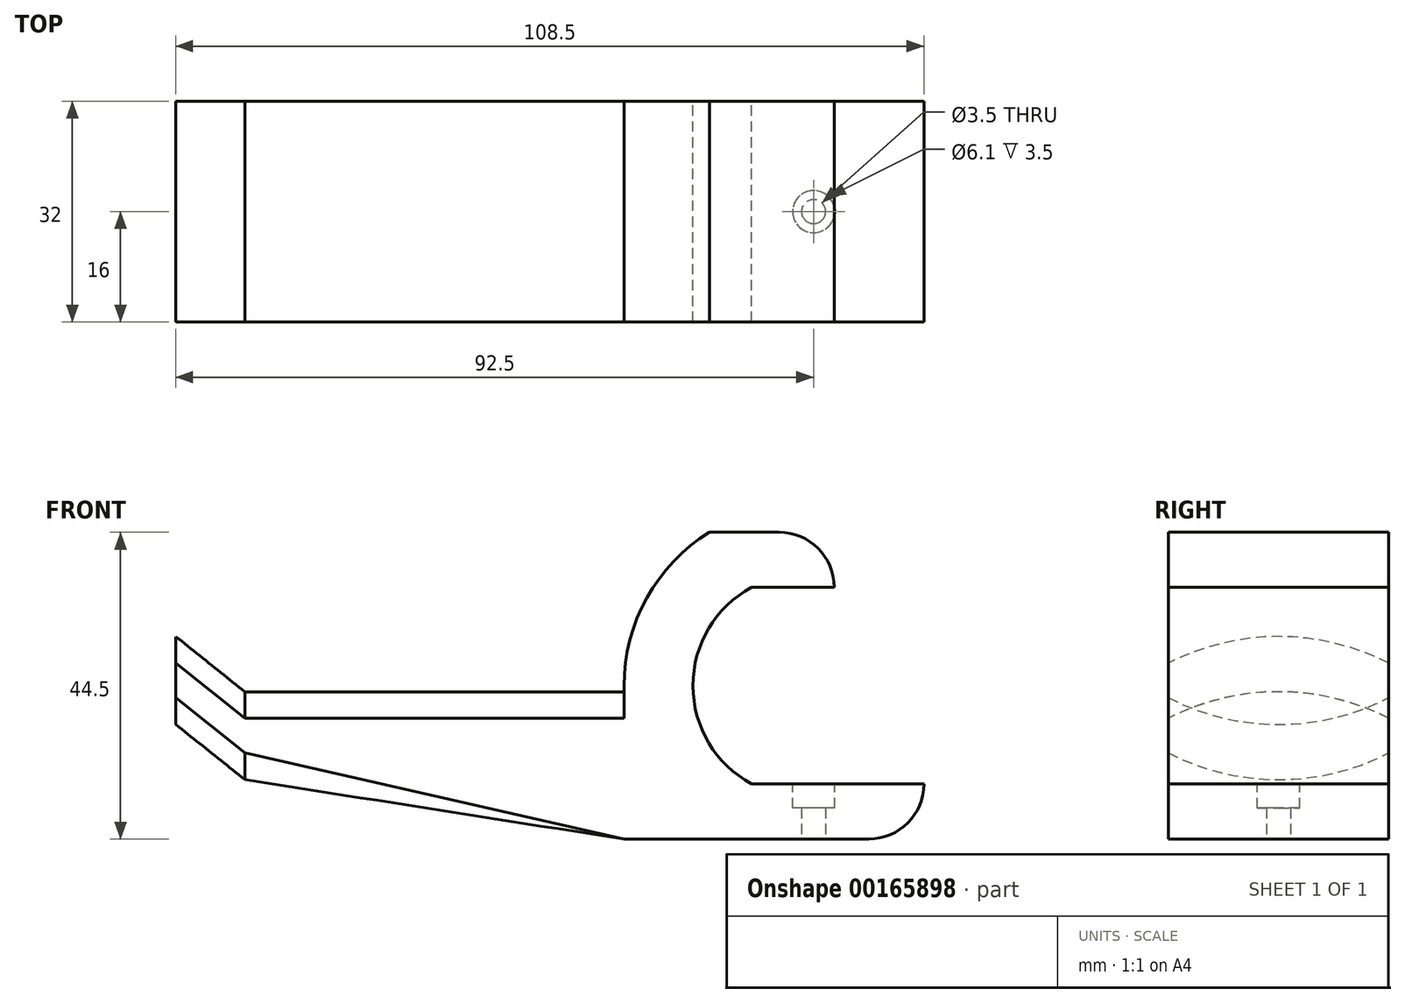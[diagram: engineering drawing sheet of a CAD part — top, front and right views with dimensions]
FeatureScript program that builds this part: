
annotation { "Feature Type Name" : "Feature", "Feature Type Description" : "" }
export const myFeature = defineFeature(function(context is Context, id is Id, definition is map)
    precondition{}
    {
        {
            var Q0;
            Q0=qCreatedBy(makeId("Front.planeOp"),FACE);
            var sketch = newSketch(context, id + "F0", { "sketchPlane" : qUnion([Q0])});
            skArc(sketch, "E0", {"start": v(8.5, 14.25) * mm, "mid": v(0, 0) * mm, "end": v(8.5, -14.25) * mm});
            skLineSegment(sketch, "E1", {"start": v(8.5, 14.25) * mm, "end": v(20.5, 14.25) * mm});
            skLineSegment(sketch, "E2", {"start": v(8.5, -14.25) * mm, "end": v(33.5, -14.25) * mm});
            skArc(sketch, "E3", {"start": v(20.5, 14.25) * mm, "mid": v(18.16, 19.9) * mm, "end": v(12.5, 22.25) * mm});
            skLineSegment(sketch, "E4", {"start": v(12.5, 22.25) * mm, "end": v(2.37, 22.25) * mm});
            skArc(sketch, "E5", {"start": v(2.37, 22.25) * mm, "mid": v(-6.7, 12.73) * mm, "end": v(-10, 0) * mm});
            skArc(sketch, "E6", {"start": v(25.5, -22.25) * mm, "mid": v(31.16, -19.9) * mm, "end": v(33.5, -14.25) * mm});
            skLineSegment(sketch, "E7", {"start": v(25.5, -22.25) * mm, "end": v(-10, -22.25) * mm});
            skLineSegment(sketch, "E8", {"start": v(-10, 0) * mm, "end": v(-10, -22.25) * mm});
            skSolve(sketch);
        }
        {
            var Q0;
            Q0 = qSketchRegion(id + "F0", true);
            extrude(context, id + "F1", {"entities" : qUnion([Q0]), "depth" : 16 * mm, "hasSecondDirection" : true, "secondDirectionOppositeDirection" : true, "secondDirectionDepth" : 16 * mm});
        }
        {
            var Q0;
            Q0=makeQuery(id+"F1.opExtrude","SWEPT_FACE",FACE,{"disambiguationData":[OSD([sQuery(id+"F0.wireOp",EDGE,"E8")])]});
            var sketch = newSketch(context, id + "F2", { "sketchPlane" : qUnion([Q0])});
            skArc(sketch, "E9", {"start": v(16, -4.75) * mm, "mid": v(0, -0.88) * mm, "end": v(-16, -4.75) * mm});
            skLineSegment(sketch, "E10", {"start": v(16, -4.75) * mm, "end": v(16, -9.75) * mm});
            skLineSegment(sketch, "E11", {"start": v(-16, -9.75) * mm, "end": v(-16, -4.75) * mm});
            skArc(sketch, "E12", {"start": v(-16, -9.75) * mm, "mid": v(0, -13.62) * mm, "end": v(16, -9.75) * mm});
            skSolve(sketch);
        }
        {
            var Q0;
            Q0 = qSketchRegion(id + "F2", true);
            extrude(context, id + "F3", {"entities" : qUnion([Q0]), "operationType" : NewBodyOperationType.ADD, "depth" : 55 * mm});
        }
        {
            var Q0;
            Q0=makeQuery(id+"F3.opExtrude","CAP_FACE",FACE,{"disambiguationData":[OSD([sQuery(id+"F2.wireOp",EDGE,"E9"),sQuery(id+"F2.wireOp",EDGE,"6S7h7Q65-Thhc-JWmT-00Su-hTCSwhGGrYMq")])],"isStart":false});
            cPlane(context, id + "F4", {"entities" : qUnion([Q0]), "cplaneType" : CPlaneType.OFFSET, "offset" : 10 * mm, "width" : 150 * mm, "height" : 150 * mm});
        }
        {
            var Q1;
            {var subQ0=sQuery(id+"F0.wireOp",EDGE,"E7");var subQ1=sQuery(id+"F0.wireOp",EDGE,"E8");Q1=makeQuery(id+"F3.boolean.opBoolean","SPLIT",FACE,{"disambiguationData":[TD([makeQuery(id+"F1.opExtrude","SWEPT_FACE",FACE,{"disambiguationData":[OSD([subQ0])]})])],"derivedFrom":makeQuery(id+"F1.opExtrude","SWEPT_FACE",FACE,{"disambiguationData":[OSD([subQ1])]})});}
            var Q2;
            Q2=makeQuery(id+"F3.opExtrude","CAP_FACE",FACE,{"disambiguationData":[OSD([sQuery(id+"F2.wireOp",EDGE,"E9"),sQuery(id+"F2.wireOp",EDGE,"E10"),sQuery(id+"F2.wireOp",EDGE,"E11"),sQuery(id+"F2.wireOp",EDGE,"E12")])],"isStart":false});
            loft(context, id + "F5", {"operationType" : NewBodyOperationType.ADD, "sheetProfilesArray" : [{ "sheetProfileEntities" : qUnion([Q1]) }, { "sheetProfileEntities" : qUnion([Q2]) }]});
        }
        {
            var Q0;
            Q0=qCreatedBy(id+"F4.planeOp",FACE);
            var sketch = newSketch(context, id + "F6", { "sketchPlane" : qUnion([Q0])});
            skLineSegment(sketch, "E13", {"start": v(16, -1.75) * mm, "end": v(16, 3.25) * mm});
            skLineSegment(sketch, "E14", {"start": v(-16, -1.75) * mm, "end": v(-16, 3.25) * mm});
            skArc(sketch, "E15", {"start": v(16, 3.25) * mm, "mid": v(0, 7.12) * mm, "end": v(-16, 3.25) * mm});
            skPoint(sketch, "E16", {"position": v(16, -4.75) * mm});
            skPoint(sketch, "E17", {"position": v(-16, -4.75) * mm});
            skArc(sketch, "E18", {"start": v(-16, -1.75) * mm, "mid": v(0, -5.62) * mm, "end": v(16, -1.75) * mm});
            skSolve(sketch);
        }
        {
            var Q1;
            Q1=makeQuery(id+"F3.opExtrude","CAP_FACE",FACE,{"disambiguationData":[OSD([sQuery(id+"F2.wireOp",EDGE,"E9"),sQuery(id+"F2.wireOp",EDGE,"6S7h7Q65-Thhc-JWmT-00Su-hTCSwhGGrYMq")])],"isStart":false});
            var Q2;
            Q2=makeQuery(id+"F6.imprint","IMPRINT",FACE,{"disambiguationData":[TD([[makeQuery(id+"F6.imprint","IMPRINT",EDGE,{"derivedFrom":sQuery(id+"F6.wireOp",EDGE,"E13")}),1.0]])]});
            loft(context, id + "F7", {"operationType" : NewBodyOperationType.ADD, "sheetProfilesArray" : [{ "sheetProfileEntities" : qUnion([Q1]) }, { "sheetProfileEntities" : qUnion([Q2]) }]});
        }
        {
            var Q0;
            Q0=makeQuery(id+"F1.opExtrude","SWEPT_FACE",FACE,{"disambiguationData":[OSD([sQuery(id+"F0.wireOp",EDGE,"E7")])]});
            var sketch = newSketch(context, id + "F8", { "sketchPlane" : qUnion([Q0])});
            skPoint(sketch, "E19", {"position": v(8.5, 0) * mm});
            skCircle(sketch, "E20", {"center": v(17.5, 0) * mm, "radius": 1.75 * mm});
            skSolve(sketch);
        }
        {
            var Q0;
            Q0 = qSketchRegion(id + "F8", true);
            extrude(context, id + "F9", {"entities" : qUnion([Q0]), "operationType" : NewBodyOperationType.REMOVE, "oppositeDirection" : true, "depth" : 25 * mm});
        }
        {
            var Q0;
            Q0=makeQuery(id+"F1.opExtrude","SWEPT_FACE",FACE,{"disambiguationData":[OSD([sQuery(id+"F0.wireOp",EDGE,"E2")])]});
            var sketch = newSketch(context, id + "F10", { "sketchPlane" : qUnion([Q0])});
            skCircle(sketch, "E21", {"center": v(17.5, 0) * mm, "radius": 3.05 * mm});
            skSolve(sketch);
        }
        {
            var Q0;
            Q0 = qSketchRegion(id + "F10", true);
            extrude(context, id + "F11", {"entities" : qUnion([Q0]), "operationType" : NewBodyOperationType.REMOVE, "oppositeDirection" : true, "depth" : 3.5 * mm});
        }
    });
